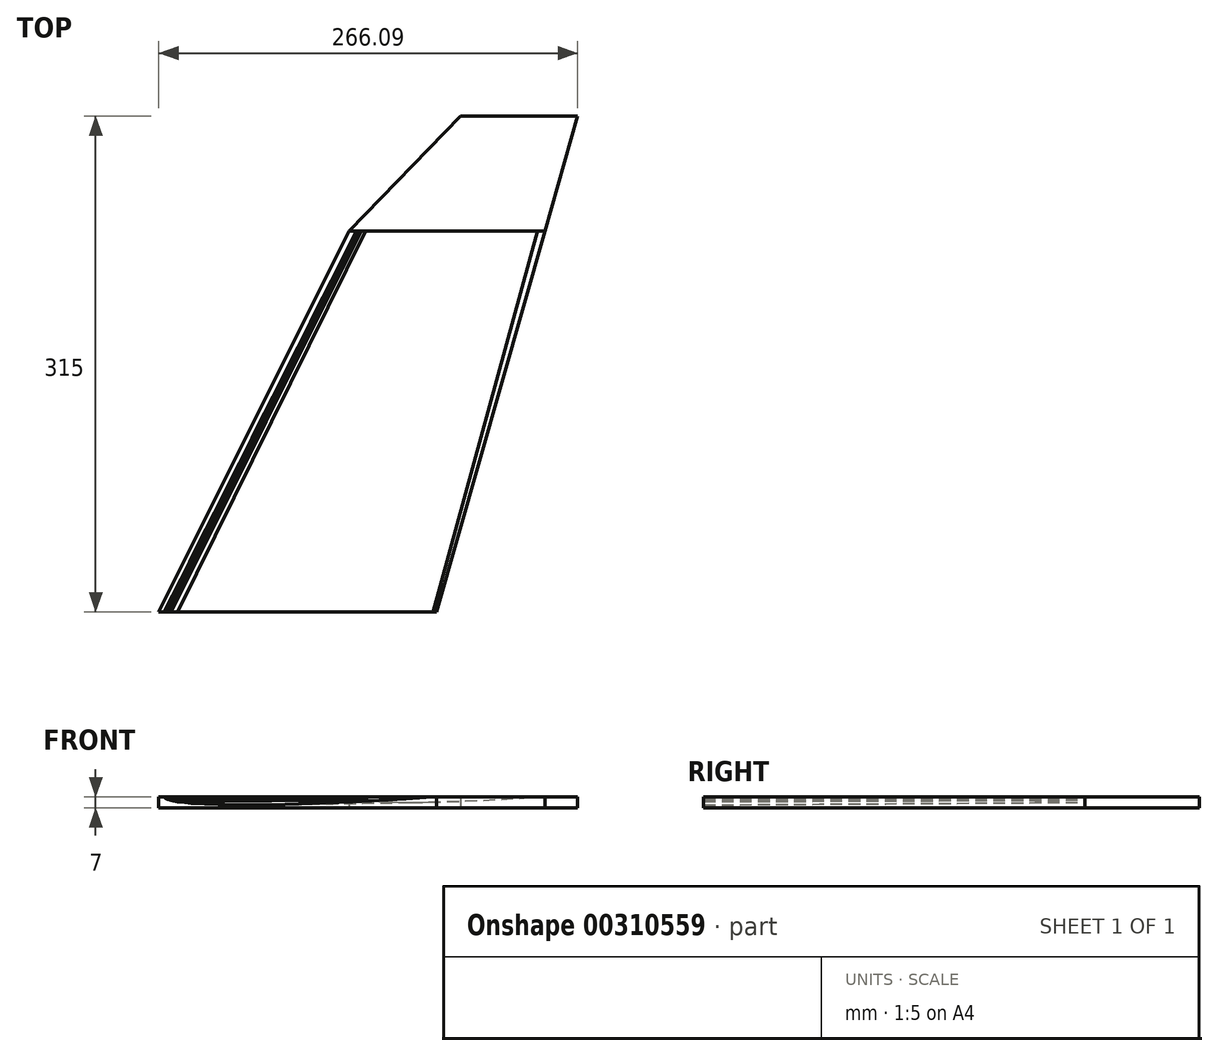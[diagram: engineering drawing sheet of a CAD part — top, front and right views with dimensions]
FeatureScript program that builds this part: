
annotation { "Feature Type Name" : "Feature", "Feature Type Description" : "" }
export const myFeature = defineFeature(function(context is Context, id is Id, definition is map)
    precondition{}
    {
        {
            var Q0;
            Q0=qCreatedBy(makeId("Front.planeOp"),FACE);
            cPlane(context, id + "F0", {"entities" : qUnion([Q0]), "cplaneType" : CPlaneType.OFFSET, "offset" : 242 * mm, "oppositeDirection" : true, "width" : 150 * mm, "height" : 150 * mm});
        }
        {
            var Q0;
            Q0=qCreatedBy(makeId("Front.planeOp"),FACE);
            cPlane(context, id + "F1", {"entities" : qUnion([Q0]), "cplaneType" : CPlaneType.OFFSET, "offset" : 315 * mm, "oppositeDirection" : true, "width" : 150 * mm, "height" : 150 * mm});
        }
        {
            var Q0;
            Q0=qCreatedBy(makeId("Front.planeOp"),FACE);
            var sketch = newSketch(context, id + "F2", { "sketchPlane" : qUnion([Q0])});
            skLineSegment(sketch, "E0", {"start": v(85.33, 0.1) * mm, "end": v(76.8, 0.69) * mm});
            skLineSegment(sketch, "E1", {"start": v(76.8, 0.69) * mm, "end": v(68.27, 1.23) * mm});
            skLineSegment(sketch, "E2", {"start": v(68.27, 1.23) * mm, "end": v(51.2, 2.24) * mm});
            skLineSegment(sketch, "E3", {"start": v(51.2, 2.24) * mm, "end": v(34.13, 3.12) * mm});
            skLineSegment(sketch, "E4", {"start": v(34.13, 3.12) * mm, "end": v(17.07, 3.9) * mm});
            skLineSegment(sketch, "E5", {"start": v(17.07, 3.9) * mm, "end": v(0, 4.51) * mm});
            skLineSegment(sketch, "E6", {"start": v(0, 4.51) * mm, "end": v(-17.07, 4.95) * mm});
            skLineSegment(sketch, "E7", {"start": v(-17.07, 4.95) * mm, "end": v(-34.13, 5.12) * mm});
            skLineSegment(sketch, "E8", {"start": v(-34.13, 5.12) * mm, "end": v(-42.67, 5.07) * mm});
            skLineSegment(sketch, "E9", {"start": v(-42.67, 5.07) * mm, "end": v(-51.2, 4.9) * mm});
            skLineSegment(sketch, "E10", {"start": v(-51.2, 4.9) * mm, "end": v(-59.73, 4.56) * mm});
            skLineSegment(sketch, "E11", {"start": v(-59.73, 4.56) * mm, "end": v(-68.27, 4) * mm});
            skLineSegment(sketch, "E12", {"start": v(-68.27, 4) * mm, "end": v(-72.53, 3.58) * mm});
            skLineSegment(sketch, "E13", {"start": v(-72.53, 3.58) * mm, "end": v(-76.8, 3.03) * mm});
            skLineSegment(sketch, "E14", {"start": v(-76.8, 3.03) * mm, "end": v(-81.07, 2.23) * mm});
            skLineSegment(sketch, "E15", {"start": v(-81.07, 2.23) * mm, "end": v(-83.2, 1.62) * mm});
            skLineSegment(sketch, "E16", {"start": v(-83.2, 1.62) * mm, "end": v(-84.61, 0.9) * mm});
            skLineSegment(sketch, "E17", {"start": v(-84.61, 0.9) * mm, "end": v(-85.33, 0) * mm});
            skLineSegment(sketch, "E18", {"start": v(-85.33, 0) * mm, "end": v(-84.68, -0.91) * mm});
            skLineSegment(sketch, "E19", {"start": v(-84.68, -0.91) * mm, "end": v(-83.2, -1.62) * mm});
            skLineSegment(sketch, "E20", {"start": v(-83.2, -1.62) * mm, "end": v(-81.07, -2.23) * mm});
            skLineSegment(sketch, "E21", {"start": v(-81.07, -2.23) * mm, "end": v(-76.8, -3.03) * mm});
            skLineSegment(sketch, "E22", {"start": v(-76.8, -3.03) * mm, "end": v(-72.53, -3.58) * mm});
            skLineSegment(sketch, "E23", {"start": v(-72.53, -3.58) * mm, "end": v(-68.27, -4) * mm});
            skLineSegment(sketch, "E24", {"start": v(-68.27, -4) * mm, "end": v(-59.73, -4.56) * mm});
            skLineSegment(sketch, "E25", {"start": v(-59.73, -4.56) * mm, "end": v(-51.2, -4.9) * mm});
            skLineSegment(sketch, "E26", {"start": v(-51.2, -4.9) * mm, "end": v(-42.67, -5.07) * mm});
            skLineSegment(sketch, "E27", {"start": v(-42.67, -5.07) * mm, "end": v(-34.13, -5.12) * mm});
            skLineSegment(sketch, "E28", {"start": v(-34.13, -5.12) * mm, "end": v(-17.07, -4.95) * mm});
            skLineSegment(sketch, "E29", {"start": v(-17.07, -4.95) * mm, "end": v(0, -4.51) * mm});
            skLineSegment(sketch, "E30", {"start": v(0, -4.51) * mm, "end": v(17.07, -3.9) * mm});
            skLineSegment(sketch, "E31", {"start": v(17.07, -3.9) * mm, "end": v(34.13, -3.12) * mm});
            skLineSegment(sketch, "E32", {"start": v(34.13, -3.12) * mm, "end": v(51.2, -2.24) * mm});
            skLineSegment(sketch, "E33", {"start": v(51.2, -2.24) * mm, "end": v(68.27, -1.23) * mm});
            skLineSegment(sketch, "E34", {"start": v(68.27, -1.23) * mm, "end": v(76.8, -0.69) * mm});
            skLineSegment(sketch, "E35", {"start": v(76.8, -0.69) * mm, "end": v(85.33, -0.1) * mm});
            skLineSegment(sketch, "E36", {"start": v(85.33, -0.1) * mm, "end": v(85.33, 0.1) * mm});
            skSolve(sketch);
        }
        {
            var Q0;
            Q0=qCreatedBy(id+"F0.planeOp",FACE);
            var sketch = newSketch(context, id + "F3", { "sketchPlane" : qUnion([Q0])});
            skLineSegment(sketch, "E37", {"start": v(151.77, 0.06) * mm, "end": v(146.02, 0.44) * mm});
            skLineSegment(sketch, "E38", {"start": v(146.02, 0.44) * mm, "end": v(140.27, 0.8) * mm});
            skLineSegment(sketch, "E39", {"start": v(140.27, 0.8) * mm, "end": v(128.77, 1.48) * mm});
            skLineSegment(sketch, "E40", {"start": v(128.77, 1.48) * mm, "end": v(117.27, 2.07) * mm});
            skLineSegment(sketch, "E41", {"start": v(117.27, 2.07) * mm, "end": v(105.77, 2.58) * mm});
            skLineSegment(sketch, "E42", {"start": v(105.77, 2.58) * mm, "end": v(94.27, 3) * mm});
            skLineSegment(sketch, "E43", {"start": v(94.27, 3) * mm, "end": v(82.77, 3.28) * mm});
            skLineSegment(sketch, "E44", {"start": v(82.77, 3.28) * mm, "end": v(71.27, 3.4) * mm});
            skLineSegment(sketch, "E45", {"start": v(71.27, 3.4) * mm, "end": v(65.52, 3.36) * mm});
            skLineSegment(sketch, "E46", {"start": v(65.52, 3.36) * mm, "end": v(59.77, 3.24) * mm});
            skLineSegment(sketch, "E47", {"start": v(59.77, 3.24) * mm, "end": v(54.02, 3.02) * mm});
            skLineSegment(sketch, "E48", {"start": v(54.02, 3.02) * mm, "end": v(48.27, 2.64) * mm});
            skLineSegment(sketch, "E49", {"start": v(48.27, 2.64) * mm, "end": v(45.4, 2.37) * mm});
            skLineSegment(sketch, "E50", {"start": v(45.4, 2.37) * mm, "end": v(42.52, 2) * mm});
            skLineSegment(sketch, "E51", {"start": v(42.52, 2) * mm, "end": v(39.65, 1.47) * mm});
            skLineSegment(sketch, "E52", {"start": v(39.65, 1.47) * mm, "end": v(38.2, 1.06) * mm});
            skLineSegment(sketch, "E53", {"start": v(38.2, 1.06) * mm, "end": v(37.26, 0.58) * mm});
            skLineSegment(sketch, "E54", {"start": v(37.26, 0.58) * mm, "end": v(36.77, -0.01) * mm});
            skLineSegment(sketch, "E55", {"start": v(36.77, -0.01) * mm, "end": v(37.21, -0.62) * mm});
            skLineSegment(sketch, "E56", {"start": v(37.21, -0.62) * mm, "end": v(38.2, -1.09) * mm});
            skLineSegment(sketch, "E57", {"start": v(38.2, -1.09) * mm, "end": v(39.65, -1.5) * mm});
            skLineSegment(sketch, "E58", {"start": v(39.65, -1.5) * mm, "end": v(42.52, -2.03) * mm});
            skLineSegment(sketch, "E59", {"start": v(42.52, -2.03) * mm, "end": v(45.4, -2.4) * mm});
            skLineSegment(sketch, "E60", {"start": v(45.4, -2.4) * mm, "end": v(48.27, -2.67) * mm});
            skLineSegment(sketch, "E61", {"start": v(48.27, -2.67) * mm, "end": v(54.02, -3.05) * mm});
            skLineSegment(sketch, "E62", {"start": v(54.02, -3.05) * mm, "end": v(59.77, -3.27) * mm});
            skLineSegment(sketch, "E63", {"start": v(59.77, -3.27) * mm, "end": v(65.52, -3.38) * mm});
            skLineSegment(sketch, "E64", {"start": v(65.52, -3.38) * mm, "end": v(71.27, -3.42) * mm});
            skLineSegment(sketch, "E65", {"start": v(71.27, -3.42) * mm, "end": v(82.77, -3.3) * mm});
            skLineSegment(sketch, "E66", {"start": v(82.77, -3.3) * mm, "end": v(94.27, -3.02) * mm});
            skLineSegment(sketch, "E67", {"start": v(94.27, -3.02) * mm, "end": v(105.77, -2.6) * mm});
            skLineSegment(sketch, "E68", {"start": v(105.77, -2.6) * mm, "end": v(117.27, -2.1) * mm});
            skLineSegment(sketch, "E69", {"start": v(117.27, -2.1) * mm, "end": v(128.77, -1.5) * mm});
            skLineSegment(sketch, "E70", {"start": v(128.77, -1.5) * mm, "end": v(140.27, -0.83) * mm});
            skLineSegment(sketch, "E71", {"start": v(140.27, -0.83) * mm, "end": v(146.02, -0.47) * mm});
            skLineSegment(sketch, "E72", {"start": v(146.02, -0.47) * mm, "end": v(151.77, -0.08) * mm});
            skLineSegment(sketch, "E73", {"start": v(151.77, -0.08) * mm, "end": v(151.77, 0.06) * mm});
            skSolve(sketch);
        }
        {
            var Q0;
            Q0=qCreatedBy(id+"F1.planeOp",FACE);
            var sketch = newSketch(context, id + "F4", { "sketchPlane" : qUnion([Q0])});
            skLineSegment(sketch, "E74", {"start": v(172.88, 0.04) * mm, "end": v(169.63, 0.25) * mm});
            skLineSegment(sketch, "E75", {"start": v(169.63, 0.25) * mm, "end": v(166.37, 0.45) * mm});
            skLineSegment(sketch, "E76", {"start": v(166.37, 0.45) * mm, "end": v(159.87, 0.82) * mm});
            skLineSegment(sketch, "E77", {"start": v(159.87, 0.82) * mm, "end": v(153.36, 1.14) * mm});
            skLineSegment(sketch, "E78", {"start": v(153.36, 1.14) * mm, "end": v(146.85, 1.42) * mm});
            skLineSegment(sketch, "E79", {"start": v(146.85, 1.42) * mm, "end": v(140.34, 1.65) * mm});
            skLineSegment(sketch, "E80", {"start": v(140.34, 1.65) * mm, "end": v(133.83, 1.8) * mm});
            skLineSegment(sketch, "E81", {"start": v(133.83, 1.8) * mm, "end": v(127.33, 1.87) * mm});
            skLineSegment(sketch, "E82", {"start": v(127.33, 1.87) * mm, "end": v(124.07, 1.85) * mm});
            skLineSegment(sketch, "E83", {"start": v(124.07, 1.85) * mm, "end": v(120.82, 1.79) * mm});
            skLineSegment(sketch, "E84", {"start": v(120.82, 1.79) * mm, "end": v(117.56, 1.67) * mm});
            skLineSegment(sketch, "E85", {"start": v(117.56, 1.67) * mm, "end": v(114.31, 1.46) * mm});
            skLineSegment(sketch, "E86", {"start": v(114.31, 1.46) * mm, "end": v(112.68, 1.3) * mm});
            skLineSegment(sketch, "E87", {"start": v(112.68, 1.3) * mm, "end": v(111.06, 1.1) * mm});
            skLineSegment(sketch, "E88", {"start": v(111.06, 1.1) * mm, "end": v(109.43, 0.81) * mm});
            skLineSegment(sketch, "E89", {"start": v(109.43, 0.81) * mm, "end": v(108.62, 0.6) * mm});
            skLineSegment(sketch, "E90", {"start": v(108.62, 0.6) * mm, "end": v(108.08, 0.33) * mm});
            skLineSegment(sketch, "E91", {"start": v(108.2, 0.47) * mm, "end": v(107.8, 0) * mm});
            skLineSegment(sketch, "E92", {"start": v(107.8, 0) * mm, "end": v(108.05, -0.33) * mm});
            skLineSegment(sketch, "E93", {"start": v(108.05, -0.33) * mm, "end": v(108.62, -0.6) * mm});
            skLineSegment(sketch, "E94", {"start": v(108.62, -0.6) * mm, "end": v(109.43, -0.81) * mm});
            skLineSegment(sketch, "E95", {"start": v(109.43, -0.81) * mm, "end": v(111.06, -1.1) * mm});
            skLineSegment(sketch, "E96", {"start": v(111.06, -1.1) * mm, "end": v(112.68, -1.3) * mm});
            skLineSegment(sketch, "E97", {"start": v(112.68, -1.3) * mm, "end": v(114.31, -1.46) * mm});
            skLineSegment(sketch, "E98", {"start": v(114.31, -1.46) * mm, "end": v(117.56, -1.67) * mm});
            skLineSegment(sketch, "E99", {"start": v(117.56, -1.67) * mm, "end": v(120.82, -1.79) * mm});
            skLineSegment(sketch, "E100", {"start": v(120.82, -1.79) * mm, "end": v(124.07, -1.85) * mm});
            skLineSegment(sketch, "E101", {"start": v(124.07, -1.85) * mm, "end": v(127.33, -1.87) * mm});
            skLineSegment(sketch, "E102", {"start": v(127.33, -1.87) * mm, "end": v(133.83, -1.8) * mm});
            skLineSegment(sketch, "E103", {"start": v(133.83, -1.8) * mm, "end": v(140.34, -1.65) * mm});
            skLineSegment(sketch, "E104", {"start": v(140.34, -1.65) * mm, "end": v(146.85, -1.42) * mm});
            skLineSegment(sketch, "E105", {"start": v(146.85, -1.42) * mm, "end": v(153.36, -1.14) * mm});
            skLineSegment(sketch, "E106", {"start": v(153.36, -1.14) * mm, "end": v(159.87, -0.82) * mm});
            skLineSegment(sketch, "E107", {"start": v(159.87, -0.82) * mm, "end": v(166.37, -0.45) * mm});
            skLineSegment(sketch, "E108", {"start": v(166.37, -0.45) * mm, "end": v(169.63, -0.25) * mm});
            skLineSegment(sketch, "E109", {"start": v(169.63, -0.25) * mm, "end": v(172.88, -0.04) * mm});
            skLineSegment(sketch, "E110", {"start": v(172.88, -0.04) * mm, "end": v(172.88, 0.04) * mm});
            skSolve(sketch);
        }
        {
            var Q0;
            Q0=makeQuery(id+"F2.imprint","IMPRINT",FACE,{"disambiguationData":[TD([[makeQuery(id+"F2.imprint","IMPRINT",EDGE,{"derivedFrom":sQuery(id+"F2.wireOp",EDGE,"E0")}),1.0]])]});
            var Q1;
            Q1=makeQuery(id+"F3.imprint","IMPRINT",FACE,{"disambiguationData":[TD([[makeQuery(id+"F3.imprint","IMPRINT",EDGE,{"derivedFrom":sQuery(id+"F3.wireOp",EDGE,"E37")}),1.0]])]});
            loft(context, id + "F5", {"sheetProfilesArray" : [{ "sheetProfileEntities" : qUnion([Q0]) }, { "sheetProfileEntities" : qUnion([Q1]) }]});
        }
        {
            var Q0;
            Q0=qCreatedBy(makeId("Front.planeOp"),FACE);
            var sketch = newSketch(context, id + "F6", { "sketchPlane" : qUnion([Q0])});
            skLineSegment(sketch, "E111.bottom", {"start": v(-88.87, 0) * mm, "end": v(61.07, 0) * mm});
            skLineSegment(sketch, "E112.bottom", {"start": v(-88.87, 0) * mm, "end": v(87.49, 0) * mm});
            skLineSegment(sketch, "E112.top", {"start": v(-88.87, -7) * mm, "end": v(87.49, -7) * mm});
            skLineSegment(sketch, "E112.left", {"start": v(-88.87, 0) * mm, "end": v(-88.87, -7) * mm});
            skLineSegment(sketch, "E112.right", {"start": v(87.49, 0) * mm, "end": v(87.49, -7) * mm});
            skSolve(sketch);
        }
        {
            var Q0;
            Q0=qCreatedBy(id+"F0.planeOp",FACE);
            var sketch = newSketch(context, id + "F7", { "sketchPlane" : qUnion([Q0])});
            skLineSegment(sketch, "E113.bottom", {"start": v(32, 0) * mm, "end": v(156.45, 0) * mm});
            skLineSegment(sketch, "E113.top", {"start": v(32, -7) * mm, "end": v(156.45, -7) * mm});
            skLineSegment(sketch, "E113.left", {"start": v(32, 0) * mm, "end": v(32, -7) * mm});
            skLineSegment(sketch, "E113.right", {"start": v(156.45, 0) * mm, "end": v(156.45, -7) * mm});
            skSolve(sketch);
        }
        {
            var Q1;
            Q1 = qSketchRegion(id + "F3", true);
            var Q2;
            Q2=makeQuery(id+"F4.imprint","IMPRINT",FACE,{"disambiguationData":[TD([[makeQuery(id+"F4.imprint","IMPRINT",EDGE,{"derivedFrom":sQuery(id+"F4.wireOp",EDGE,"E74")}),1.0]])]});
            loft(context, id + "F8", {"operationType" : NewBodyOperationType.ADD, "sheetProfilesArray" : [{ "sheetProfileEntities" : qUnion([Q1]) }, { "sheetProfileEntities" : qUnion([Q2]) }]});
        }
        {
            var Q0;
            Q0=qCreatedBy(id+"F1.planeOp",FACE);
            var sketch = newSketch(context, id + "F9", { "sketchPlane" : qUnion([Q0])});
            skLineSegment(sketch, "E114.bottom", {"start": v(177.22, 0) * mm, "end": v(102.9, 0) * mm});
            skLineSegment(sketch, "E114.top", {"start": v(177.22, -7) * mm, "end": v(102.9, -7) * mm});
            skLineSegment(sketch, "E114.left", {"start": v(177.22, 0) * mm, "end": v(177.22, -7) * mm});
            skLineSegment(sketch, "E114.right", {"start": v(102.9, 0) * mm, "end": v(102.9, -7) * mm});
            skSolve(sketch);
        }
        {
            var Q1;
            Q1=makeQuery(id+"F6.imprint","IMPRINT",FACE,{"disambiguationData":[TD([[makeQuery(id+"F6.imprint","IMPRINT",EDGE,{"derivedFrom":sQuery(id+"F6.wireOp",EDGE,"E112.bottom")}),-1.0]])]});
            var Q2;
            Q2=makeQuery(id+"F7.imprint","IMPRINT",FACE,{"disambiguationData":[TD([[makeQuery(id+"F7.imprint","IMPRINT",EDGE,{"derivedFrom":sQuery(id+"F7.wireOp",EDGE,"E113.bottom")}),-1.0]])]});
            loft(context, id + "F10", {"sheetProfilesArray" : [{ "sheetProfileEntities" : qUnion([Q1]) }, { "sheetProfileEntities" : qUnion([Q2]) }]});
        }
        {
            var Q1;
            Q1=makeQuery(id+"F9.imprint","IMPRINT",FACE,{"disambiguationData":[TD([[makeQuery(id+"F9.imprint","IMPRINT",EDGE,{"derivedFrom":sQuery(id+"F9.wireOp",EDGE,"E114.top")}),-1.0]])]});
            var Q2;
            Q2=makeQuery(id+"F7.imprint","IMPRINT",FACE,{"disambiguationData":[TD([[makeQuery(id+"F7.imprint","IMPRINT",EDGE,{"derivedFrom":sQuery(id+"F7.wireOp",EDGE,"E113.bottom")}),-1.0]])]});
            loft(context, id + "F11", {"sheetProfilesArray" : [{ "sheetProfileEntities" : qUnion([Q1]) }, { "sheetProfileEntities" : qUnion([Q2]) }]});
        }
        {
            var Q0;
            Q0=makeQuery(id+"F5.opLoft","SWEPT_BODY",BODY,{"disambiguationData":[OSD([makeQuery(id+"F2.imprint","IMPRINT",FACE,{"disambiguationData":[TD([[makeQuery(id+"F2.imprint","IMPRINT",EDGE,{"derivedFrom":sQuery(id+"F2.wireOp",EDGE,"E0")}),1.0]])]}),makeQuery(id+"F3.imprint","IMPRINT",FACE,{"disambiguationData":[TD([[makeQuery(id+"F3.imprint","IMPRINT",EDGE,{"derivedFrom":sQuery(id+"F3.wireOp",EDGE,"E37")}),1.0]])]})])]});
            var Q1;
            Q1=makeQuery(id+"F10.opLoft","SWEPT_BODY",BODY,{"disambiguationData":[OSD([makeQuery(id+"F6.imprint","IMPRINT",FACE,{"disambiguationData":[TD([[makeQuery(id+"F6.imprint","IMPRINT",EDGE,{"derivedFrom":sQuery(id+"F6.wireOp",EDGE,"E112.bottom")}),-1.0]])]}),makeQuery(id+"F7.imprint","IMPRINT",FACE,{"disambiguationData":[TD([[makeQuery(id+"F7.imprint","IMPRINT",EDGE,{"derivedFrom":sQuery(id+"F7.wireOp",EDGE,"E113.bottom")}),-1.0]])]})])]});
            booleanBodies(context, id + "F12", {"operationType" : BooleanOperationType.SUBTRACTION, "tools" : qUnion([Q0]), "targets" : qUnion([Q1])});
        }
    });
